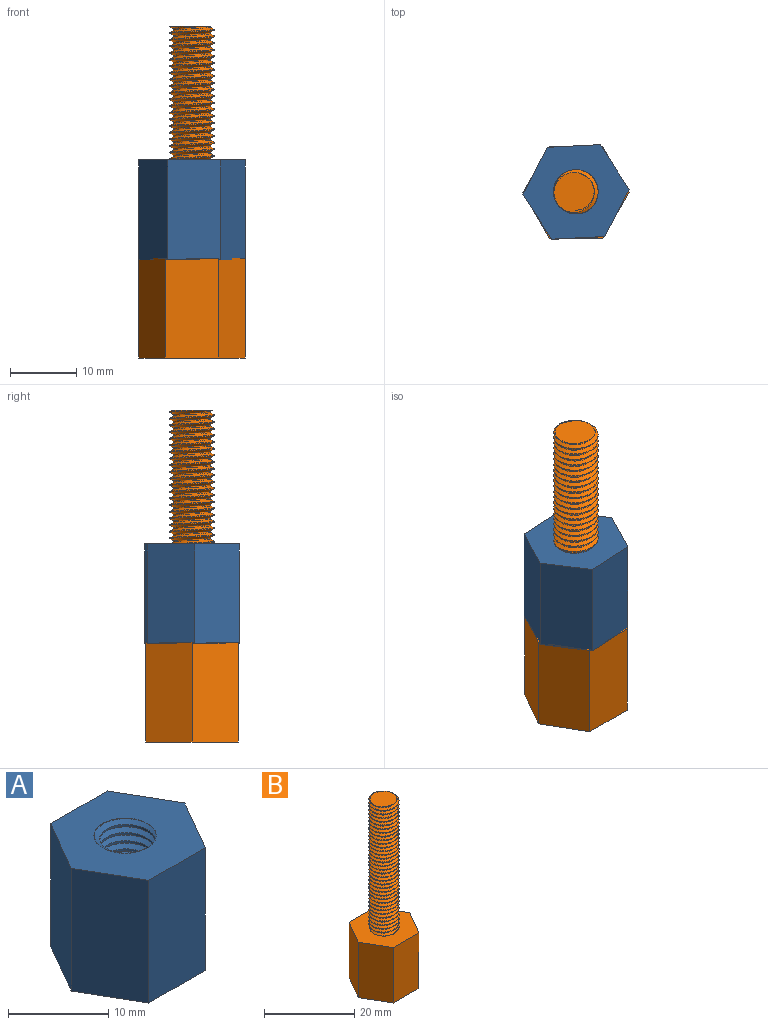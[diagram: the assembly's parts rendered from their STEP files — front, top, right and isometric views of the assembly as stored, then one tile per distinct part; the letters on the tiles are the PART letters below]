
ASSEMBLY  parts=2 mates=1
PART A: 12 faces, bbox 16.3x14.1x16.1 mm
  f0: plane 16.29x14.15mm, normal (0,0,-1), area 136.6mm2, adj f2,f3,f4,f5,f6,f7,f8,f9
  f1: plane 16.29x14.15mm, normal (0,0,1), area 136.6mm2, adj f2,f3,f4,f5,f6,f7,f8,f9
  f2: plane 15x6.93mm, normal (0.87,-0.5,0), area 120mm2, adj f0,f1,f3,f7
  f3: plane 15x6.93mm, normal (0.87,0.5,0), area 120mm2, adj f0,f1,f2,f4
  f4: plane 15x8mm, normal (0,1,0), area 120mm2, adj f0,f1,f3,f5
  f5: plane 15x6.93mm, normal (-0.87,0.5,0), area 120mm2, adj f0,f1,f4,f6
  f6: plane 15x6.93mm, normal (-0.87,-0.5,0), area 120mm2, adj f0,f1,f5,f7
  f7: plane 15x8mm, normal (0,-1,0), area 120mm2, adj f0,f1,f2,f6
  f8: bspline ~15.65x7.77mm, area 182.1mm2, adj f0,f1,f10,f11
  f9: bspline ~15.81x7.77mm, area 182.7mm2, adj f0,f1,f10,f11
  f10: bspline ~15.46x7.88mm, area 46.2mm2, adj f0,f1,f8,f9
  f11: cylinder r=2.82mm len=15mm, axis (0,0,-1), area 82mm2, adj f0,f1,f8,f9
PART B: 13 faces, bbox 16.3x14.1x50.7 mm
  f0: plane 15x8mm, normal (0,1,0), area 120mm2, adj f1,f5,f6,f7
  f1: plane 15x6.93mm, normal (-0.87,0.5,0), area 120mm2, adj f0,f2,f6,f7
  f2: plane 15x6.93mm, normal (-0.87,-0.5,0), area 120mm2, adj f1,f3,f6,f7
  f3: plane 15x8mm, normal (0,-1,0), area 120mm2, adj f2,f4,f6,f7
  f4: plane 15x6.93mm, normal (0.87,-0.5,0), area 120mm2, adj f3,f5,f6,f7
  f5: plane 15x6.93mm, normal (0.87,0.5,0), area 120mm2, adj f0,f4,f6,f7
  f6: plane 16.28x14.13mm, normal (0,0,1), area 137.6mm2, adj f0,f1,f2,f3,f4,f5,f8,f10
  f7: plane 16x13.86mm, normal (0,0,-1), area 166.3mm2, adj f0,f1,f2,f3,f4,f5
  f8: cylinder r=3.32mm len=35mm, axis (0,0,-1), area 420.9mm2, adj f6,f9,f11,f12
  f9: plane 6.35x6.31mm, normal (0,0,1), area 28.6mm2, adj f8,f10,f11,f12
  f10: bspline ~35.75x6.43mm, area 168.8mm2, adj f6,f9,f11,f12
  f11: bspline ~35.81x7.68mm, area 419.8mm2, adj f6,f8,f9,f10
  f12: bspline ~35.65x7.68mm, area 421.6mm2, adj f6,f8,f9,f10
PLACE A rot(axis=(0,0,1),62.9deg) t=(0,0,-20.17)mm
PLACE B at identity fixed
MATE cylindrical A.f11 <-> B.f8  axis (0,0,1) through (0,0,29.83)mm
